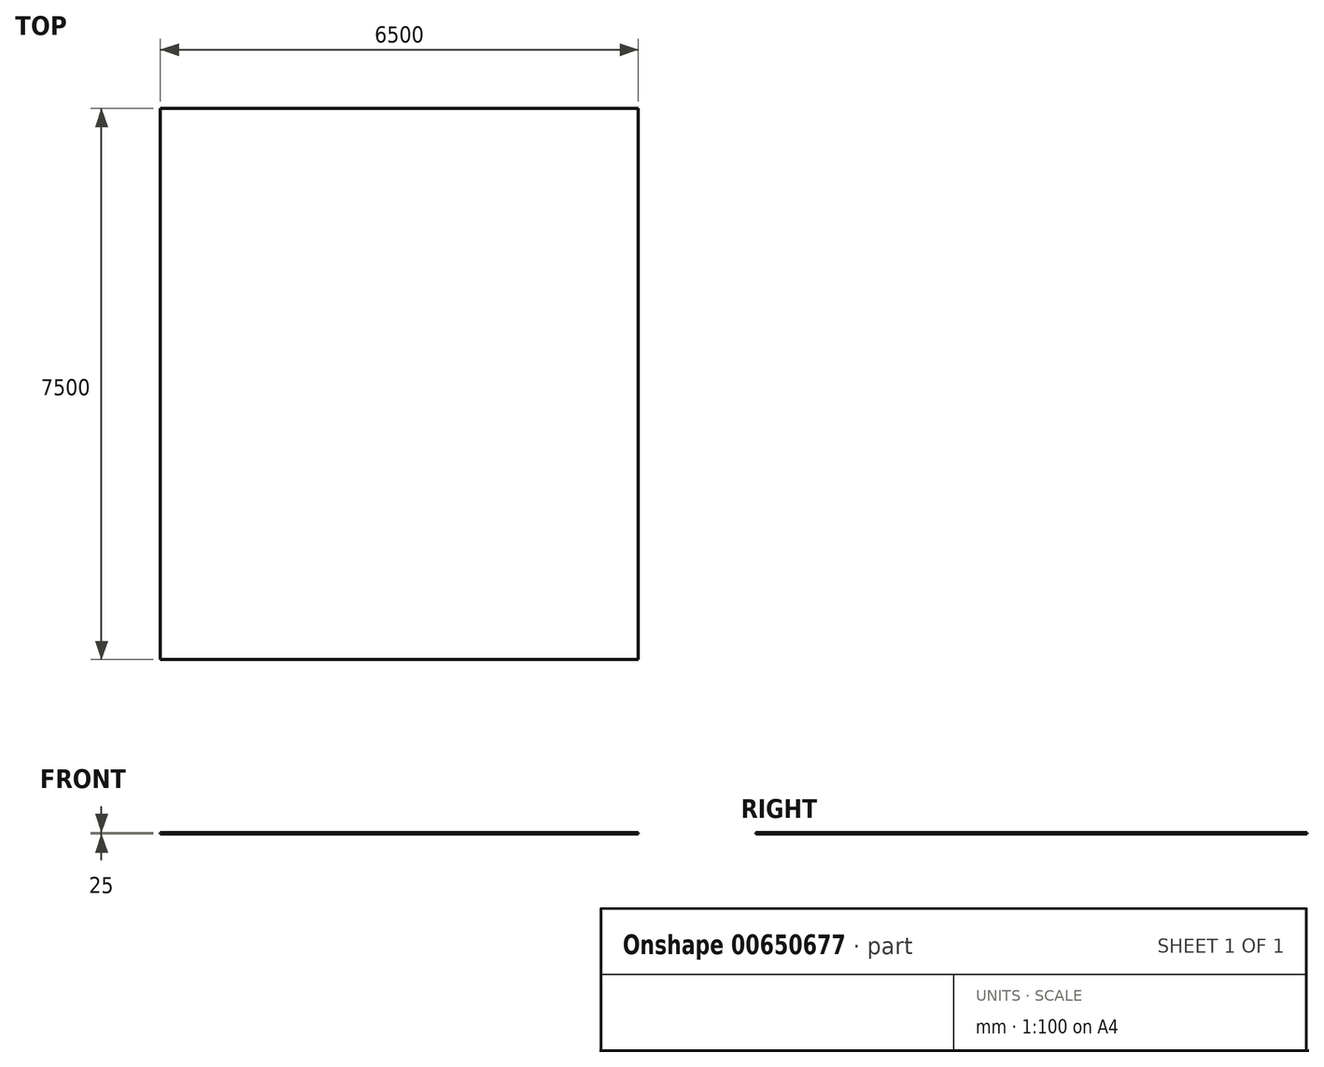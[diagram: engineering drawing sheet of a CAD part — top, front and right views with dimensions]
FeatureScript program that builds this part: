
annotation { "Feature Type Name" : "Feature", "Feature Type Description" : "" }
export const myFeature = defineFeature(function(context is Context, id is Id, definition is map)
    precondition{}
    {
        {
            var Q0;
            Q0=qCreatedBy(makeId("Top.planeOp"),FACE);
            var sketch = newSketch(context, id + "F0", { "sketchPlane" : qUnion([Q0])});
            skLineSegment(sketch, "E0.bottom", {"start": v(-3247.79, 4590.13) * mm, "end": v(3252.21, 4590.13) * mm});
            skLineSegment(sketch, "E0.top", {"start": v(-3247.79, -2909.87) * mm, "end": v(3252.21, -2909.87) * mm});
            skLineSegment(sketch, "E0.left", {"start": v(-3247.79, 4590.13) * mm, "end": v(-3247.79, -2909.87) * mm});
            skLineSegment(sketch, "E0.right", {"start": v(3252.21, 4590.13) * mm, "end": v(3252.21, -2909.87) * mm});
            skSolve(sketch);
        }
        {
            var Q0;
            Q0 = qSketchRegion(id + "F0", true);
            extrude(context, id + "F1", {"entities" : qUnion([Q0]), "depth" : 25 * mm, "offsetDistance" : 25 * mm});
        }
    });
